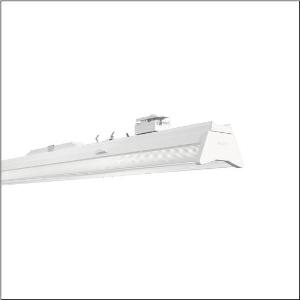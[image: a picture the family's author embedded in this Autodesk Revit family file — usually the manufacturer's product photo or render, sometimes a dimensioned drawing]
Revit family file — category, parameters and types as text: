
# Revit family: licross_r__21_performance_mo_52td16vn455g_74b2
name_source: partatom
category: Lighting Fixtures
units: mm (PartAtom-declared; Revit-internal decimal feet)

## family parameters
Cut with Voids When Loaded = No
Host = Face
Light Source = No
Part Type = Normal
Room Calculation Point = No
Round Connector Dimension = Use Diameter
Shared = No

## types (1)
- --- (1 x LED, 5500 lm, 30 W, 4000K)
    Apparent Load = 30 VA
    CIE Flux Codes = 66 88 96 79 100
    Color Rendering = 80
    Color Temperature = 4000K
    Default Elevation = 1800 mm
    Description = Licross® 21 Performance MO, luminaire insert, of sheet steel, galvanised, coil coated, white, length: 1.500mm, width: 120mm, height: 123mm, LED rated luminous flux: 5.500lm, light colour: 840, control gear: DALI 2, CLO, with plug, 5-pole, with phase selection, mains connection: 220..240V, AC, 50/60Hz, start of lifetime: 30W, end of service life: 36W, halogen-free wiring, primary light control with lens, of plastic, primary optical cover: cover, of PMMA, light emission: direct/indirect distribution, primary light characteristic: symmetric, protection rating (complete): IP54, insulation class (complete): insulation class I (protective earthing), certification: CE, ENEC, VDE, UKCA, protection symbol: D if used in an environment with non-conductive dust loads with corresponding accessories, impact resistance: IK06, permissible ambient temperature for indoor applications: -25..+50°C, corresponds to IFS (International Featured Standards) requirements for safety and quality in the food industry, reducing of maximum allowable ambient temperature of 5°C with ceiling mounting, LABS conformity tested according to VDMA 24364:2018-05, packaging unit: 1 piece
    Height = 114 mm
    Lamp = 1 x LED
    Lamp Light Flux = 5500 lm
    Lamp Power = 30 W
    Lamp count = 1
    Length = 1500 mm
    Luminous efficacy = 183 lm/W
    Manufacturer = Siteco
    ModVariant = No
    Model = 52TD16VN455G
    Mounting Place = Ceiling
    Mounting Type = Pendant
    Number of Poles = 1
    OnlyDefault = Yes
    Power Factor = 1
    Product Name = Licross® 21 Performance MO
    Product group = luminaire insert
    ProductGroupID = 901
    Protection Class = Protection class I
    Protection Degree = IP 54
    RLX_Detail_Level = 1
    RLX_Emergency_Light_Flux = 0 lm
    RLX_Emergency_Type = 0
    RLX_Emergency_Type_DB = No
    RlxData = <blob elided: 33505 chars, md5=9d9d1d30>
    Socket = socket
    Standby Power = 0 W
    System Light Flux = 5500 lm
    System Power = 30 W
    Type Comments = factory setting: luminous flux: 100 % | dim-lin: 254 | 203 mA
    Type Image = l_1256138.jpg
    URL = http://relux.com
    VarID = @adj_035341
    Voltage = 0 V
    Weight = 0.00 kg
    Width = 120 mm

## geometry (parser evidence)
native form markers: Blend x4, Sweep x12
no freeform markers — native parametric forms only
